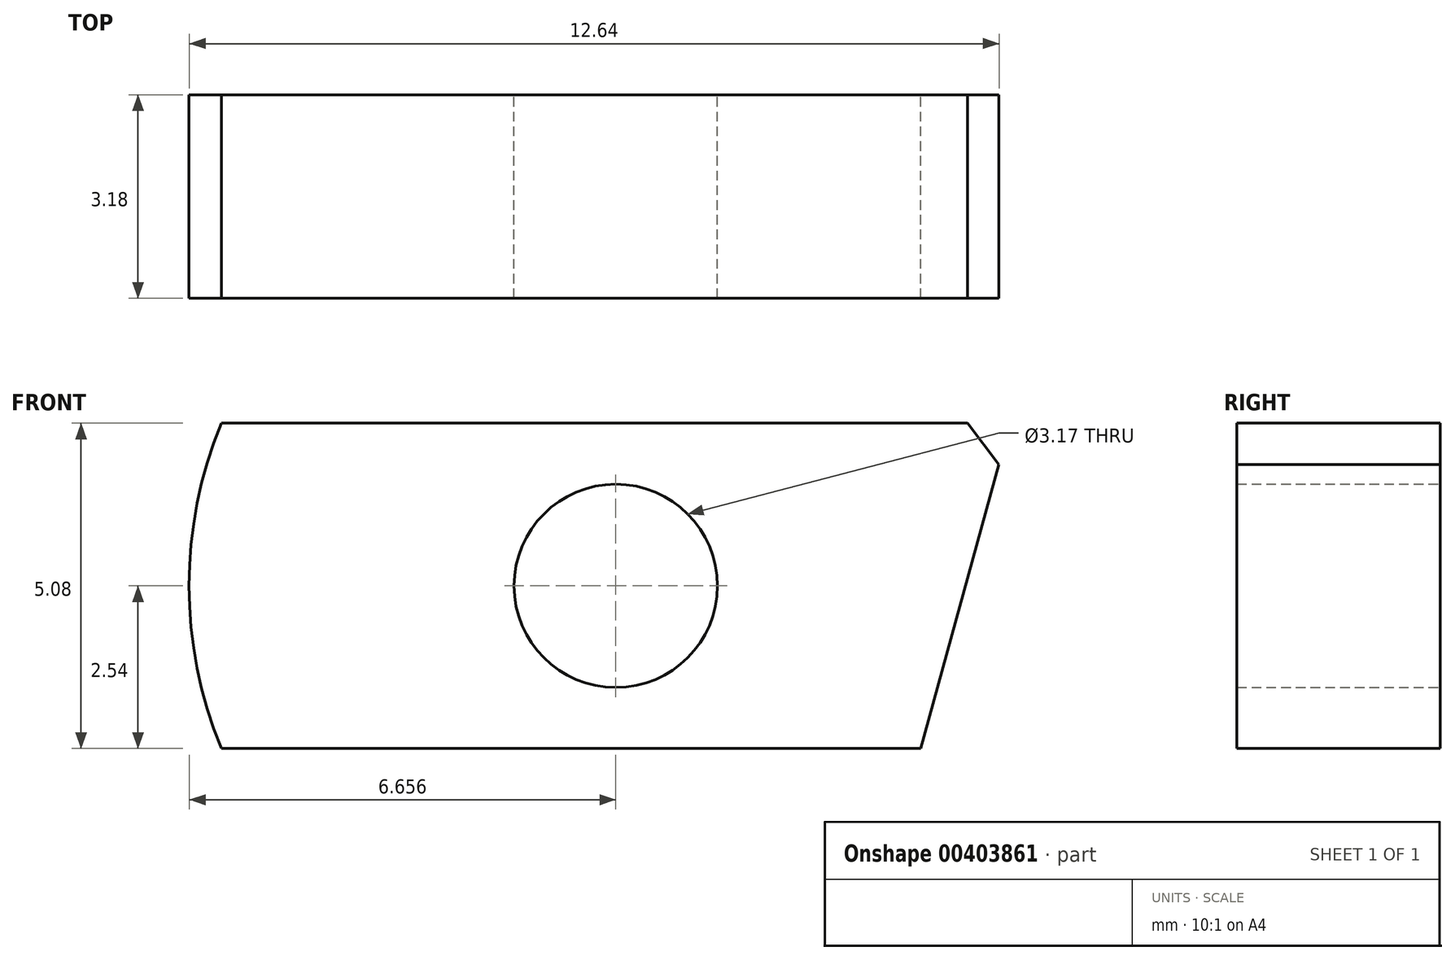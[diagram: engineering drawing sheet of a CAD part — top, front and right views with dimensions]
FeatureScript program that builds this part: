
annotation { "Feature Type Name" : "Feature", "Feature Type Description" : "" }
export const myFeature = defineFeature(function(context is Context, id is Id, definition is map)
    precondition{}
    {
        {
            var Q0;
            Q0=qCreatedBy(makeId("Front.planeOp"),FACE);
            var sketch = newSketch(context, id + "F0", { "sketchPlane" : qUnion([Q0])});
            skArc(sketch, "E0", {"start": v(-5.81, 2.54) * mm, "mid": v(-6.31, 0) * mm, "end": v(-5.81, -2.54) * mm});
            skCircle(sketch, "E1", {"center": v(0.35, 0) * mm, "radius": 1.59 * mm});
            skLineSegment(sketch, "E2", {"start": v(-5.81, 2.54) * mm, "end": v(6.5, 2.54) * mm});
            skLineSegment(sketch, "E3", {"start": v(6.5, 2.54) * mm, "end": v(5.1, -2.54) * mm});
            skLineSegment(sketch, "E4", {"start": v(-5.81, -2.54) * mm, "end": v(5.1, -2.54) * mm});
            skSolve(sketch);
        }
        {
            var Q0;
            Q0=makeQuery(id+"F0.imprint","IMPRINT",FACE,{"disambiguationData":[TD([[makeQuery(id+"F0.imprint","IMPRINT",EDGE,{"derivedFrom":sQuery(id+"F0.wireOp",EDGE,"E0")}),1.0]])]});
            extrude(context, id + "F1", {"entities" : qUnion([Q0]), "endBound" : BoundingType.SYMMETRIC, "depth" : 3.17 * mm});
        }
        {
            var Q0;
            Q0=makeQuery(id+"F1.opExtrude","SWEPT_EDGE",EDGE,{"disambiguationData":[OSD([sQuery(id+"F0.wireOp",EDGE,"E2"),sQuery(id+"F0.wireOp",EDGE,"E3")])]});
            chamfer(context, id + "F2", {"entities" : qUnion([Q0]), "width" : 0.5 * mm, "tangentPropagation" : true});
        }
    });
